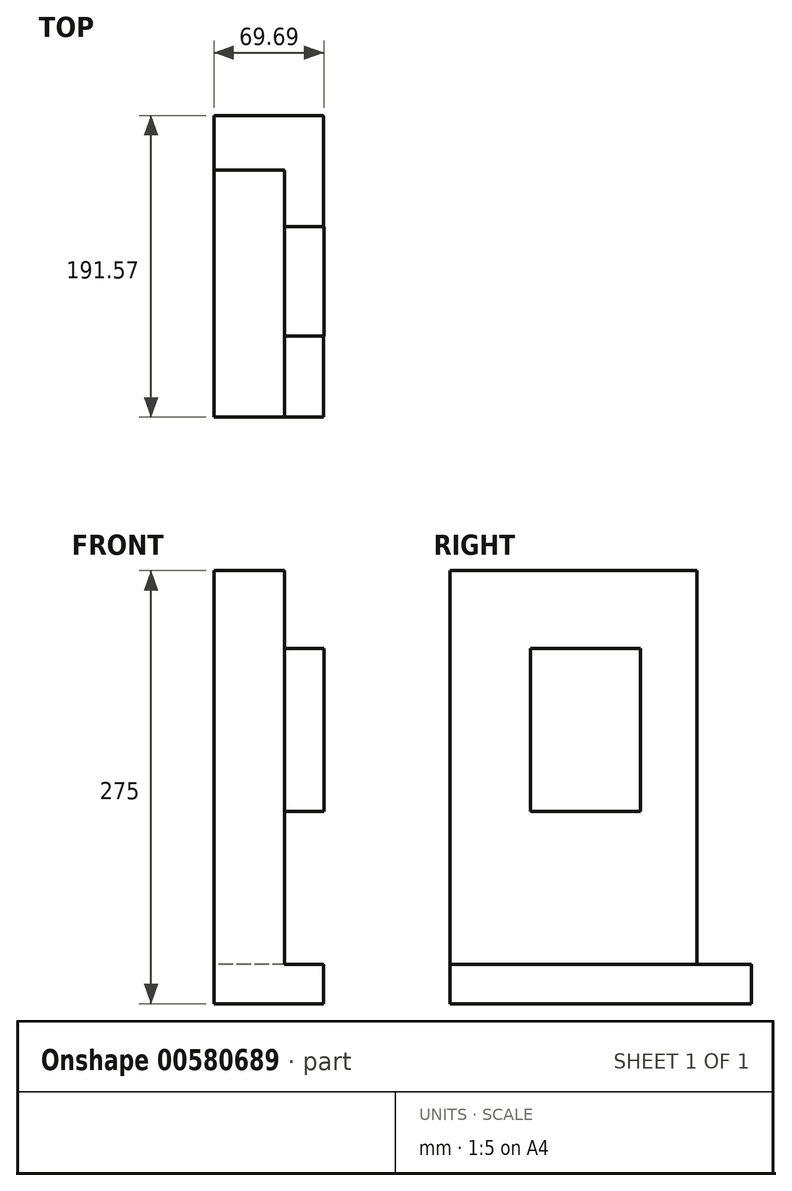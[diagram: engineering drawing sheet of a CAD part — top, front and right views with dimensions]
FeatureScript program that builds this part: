
annotation { "Feature Type Name" : "Feature", "Feature Type Description" : "" }
export const myFeature = defineFeature(function(context is Context, id is Id, definition is map)
    precondition{}
    {
        {
            var Q0;
            Q0=qCreatedBy(makeId("Top.planeOp"),FACE);
            var sketch = newSketch(context, id + "F0", { "sketchPlane" : qUnion([Q0])});
            skLineSegment(sketch, "E0", {"start": v(0, 0) * mm, "end": v(69.43, 0) * mm});
            skLineSegment(sketch, "E1", {"start": v(69.43, 0) * mm, "end": v(69.43, 70.57) * mm});
            skLineSegment(sketch, "E2", {"start": v(69.43, 70.57) * mm, "end": v(0, 70.57) * mm});
            skLineSegment(sketch, "E3", {"start": v(0, 70.57) * mm, "end": v(0, 0) * mm});
            skSolve(sketch);
        }
        {
            var Q0;
            Q0=makeQuery(id+"F0.imprint","IMPRINT",FACE,{"disambiguationData":[TD([[makeQuery(id+"F0.imprint","IMPRINT",EDGE,{"derivedFrom":sQuery(id+"F0.wireOp",EDGE,"E0")}),1.0]])]});
            extrude(context, id + "F1", {"entities" : qUnion([Q0]), "depth" : 25 * mm, "offsetDistance" : 25 * mm});
        }
        {
            var Q0;
            Q0=makeQuery(id+"F1.opExtrude","CAP_FACE",FACE,{"disambiguationData":[OSD([sQuery(id+"F0.wireOp",EDGE,"E0"),sQuery(id+"F0.wireOp",EDGE,"E1"),sQuery(id+"F0.wireOp",EDGE,"E2"),sQuery(id+"F0.wireOp",EDGE,"E3")])],"isStart":false});
            var sketch = newSketch(context, id + "F2", { "sketchPlane" : qUnion([Q0])});
            skLineSegment(sketch, "E4.bottom", {"start": v(44.69, 35.86) * mm, "end": v(0, 35.86) * mm});
            skLineSegment(sketch, "E4.top", {"start": v(44.69, 0) * mm, "end": v(0, 0) * mm});
            skLineSegment(sketch, "E4.left", {"start": v(44.69, 35.86) * mm, "end": v(44.69, 0) * mm});
            skLineSegment(sketch, "E4.right", {"start": v(0, 35.86) * mm, "end": v(0, 0) * mm});
            skSolve(sketch);
        }
        {
            var Q0;
            Q0=makeQuery(id+"F2.imprint","IMPRINT",FACE,{"disambiguationData":[TD([[makeQuery(id+"F2.imprint","IMPRINT",EDGE,{"derivedFrom":sQuery(id+"F2.wireOp",EDGE,"E4.bottom")}),1.0]])]});
            extrude(context, id + "F3", {"entities" : qUnion([Q0]), "operationType" : NewBodyOperationType.ADD, "depth" : 250 * mm, "offsetDistance" : 25 * mm});
        }
        {
            var Q0;
            Q0=makeQuery(id+"F3.boolean.opBoolean","MERGE",FACE,{"derivedFrom":[makeQuery(id+"F1.opExtrude","SWEPT_FACE",FACE,{"disambiguationData":[OSD([sQuery(id+"F0.wireOp",EDGE,"E0")])]}),makeQuery(id+"F3.opExtrude","SWEPT_FACE",FACE,{"disambiguationData":[OSD([sQuery(id+"F2.wireOp",EDGE,"E4.top")])]})]});
            extrude(context, id + "F4", {"entities" : qUnion([Q0]), "operationType" : NewBodyOperationType.ADD, "depth" : 121 * mm, "offsetDistance" : 25 * mm});
        }
        {
            var Q0;
            {var subQ0=sQuery(id+"F2.wireOp",EDGE,"E4.left");Q0=makeQuery(id+"F4.boolean.opBoolean","MERGE",FACE,{"derivedFrom":[makeQuery(id+"F3.opExtrude","SWEPT_FACE",FACE,{"disambiguationData":[OSD([subQ0])]}),makeQuery(id+"F4.opExtrude","SWEPT_FACE",FACE,{"disambiguationData":[OSD([sQuery(id+"F0.wireOp",EDGE,"E0"),sQuery(id+"F2.wireOp",EDGE,"E4.top"),subQ0])]})]});}
            var sketch = newSketch(context, id + "F5", { "sketchPlane" : qUnion([Q0])});
            skLineSegment(sketch, "E5.bottom", {"start": v(-69.6, 225.47) * mm, "end": v(0, 225.47) * mm});
            skLineSegment(sketch, "E5.top", {"start": v(-69.6, 122.14) * mm, "end": v(0, 122.14) * mm});
            skLineSegment(sketch, "E5.left", {"start": v(-69.6, 225.47) * mm, "end": v(-69.6, 122.14) * mm});
            skLineSegment(sketch, "E5.right", {"start": v(0, 225.47) * mm, "end": v(0, 122.14) * mm});
            skSolve(sketch);
        }
        {
            var Q0;
            Q0=makeQuery(id+"F5.imprint","IMPRINT",FACE,{"disambiguationData":[TD([[makeQuery(id+"F5.imprint","IMPRINT",EDGE,{"derivedFrom":sQuery(id+"F5.wireOp",EDGE,"E5.bottom")}),-1.0]])]});
            var sketch = newSketch(context, id + "F6", { "sketchPlane" : qUnion([Q0])});
            skLineSegment(sketch, "E6.bottom", {"start": v(-39.14, 167.42) * mm, "end": v(-98.62, 167.42) * mm});
            skLineSegment(sketch, "E6.top", {"start": v(-39.14, 212.06) * mm, "end": v(-98.62, 212.06) * mm});
            skLineSegment(sketch, "E6.left", {"start": v(-39.14, 167.42) * mm, "end": v(-39.14, 212.06) * mm});
            skLineSegment(sketch, "E6.right", {"start": v(-98.62, 167.42) * mm, "end": v(-98.62, 212.06) * mm});
            skSolve(sketch);
        }
        {
            var Q0;
            Q0=makeQuery(id+"F5.imprint","IMPRINT",FACE,{"disambiguationData":[TD([[makeQuery(id+"F5.imprint","IMPRINT",EDGE,{"derivedFrom":sQuery(id+"F5.wireOp",EDGE,"E5.bottom")}),-1.0]])]});
            extrude(context, id + "F7", {"entities" : qUnion([Q0]), "operationType" : NewBodyOperationType.ADD, "depth" : 25 * mm, "offsetDistance" : 25 * mm});
        }
        {
            var Q0;
            Q0=sQuery(id+"F6.wireOp",EDGE,"E6.right");
            extrude(context, id + "F8", {"bodyType" : ToolBodyType.SURFACE, "surfaceEntities" : qUnion([Q0]), "depth" : 25 * mm, "offsetDistance" : 25 * mm});
        }
    });
